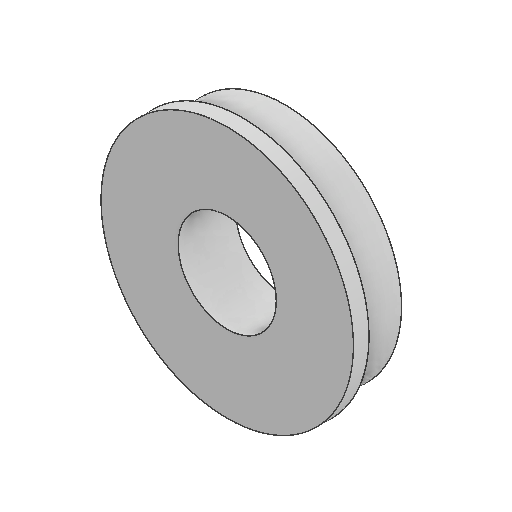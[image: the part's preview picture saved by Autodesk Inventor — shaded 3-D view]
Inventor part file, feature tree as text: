
AUTODESK INVENTOR PART (.ipt)
format: ipt  version: 2025.2 (Build 292293000, 293)  size: 115,200 bytes
history: native  units: in
note: dims shown in document units (in); Inventor stores cm internally (conversion verified against a paired STEP export)
features: extrude x2, sketch x2
ambient origin geometry x8: Origin, YZ Plane, XZ Plane, XY Plane, X Axis, Y Axis, Z Axis, Center Point
bodies: Solid1 (feature_tree)
feature tree (4):
  extrude  "Extrusion1"  Depth=0.315in
  extrude  "Extrusion2"  Depth=0.05in TaperAngle=0.0deg
  sketch  "Sketch1"  dims[d0=0.75in d1=0.315in]
  sketch  "Sketch2"  dims[d2=0.135in d3=0.0in d4=0.05in d5=0.0in]
